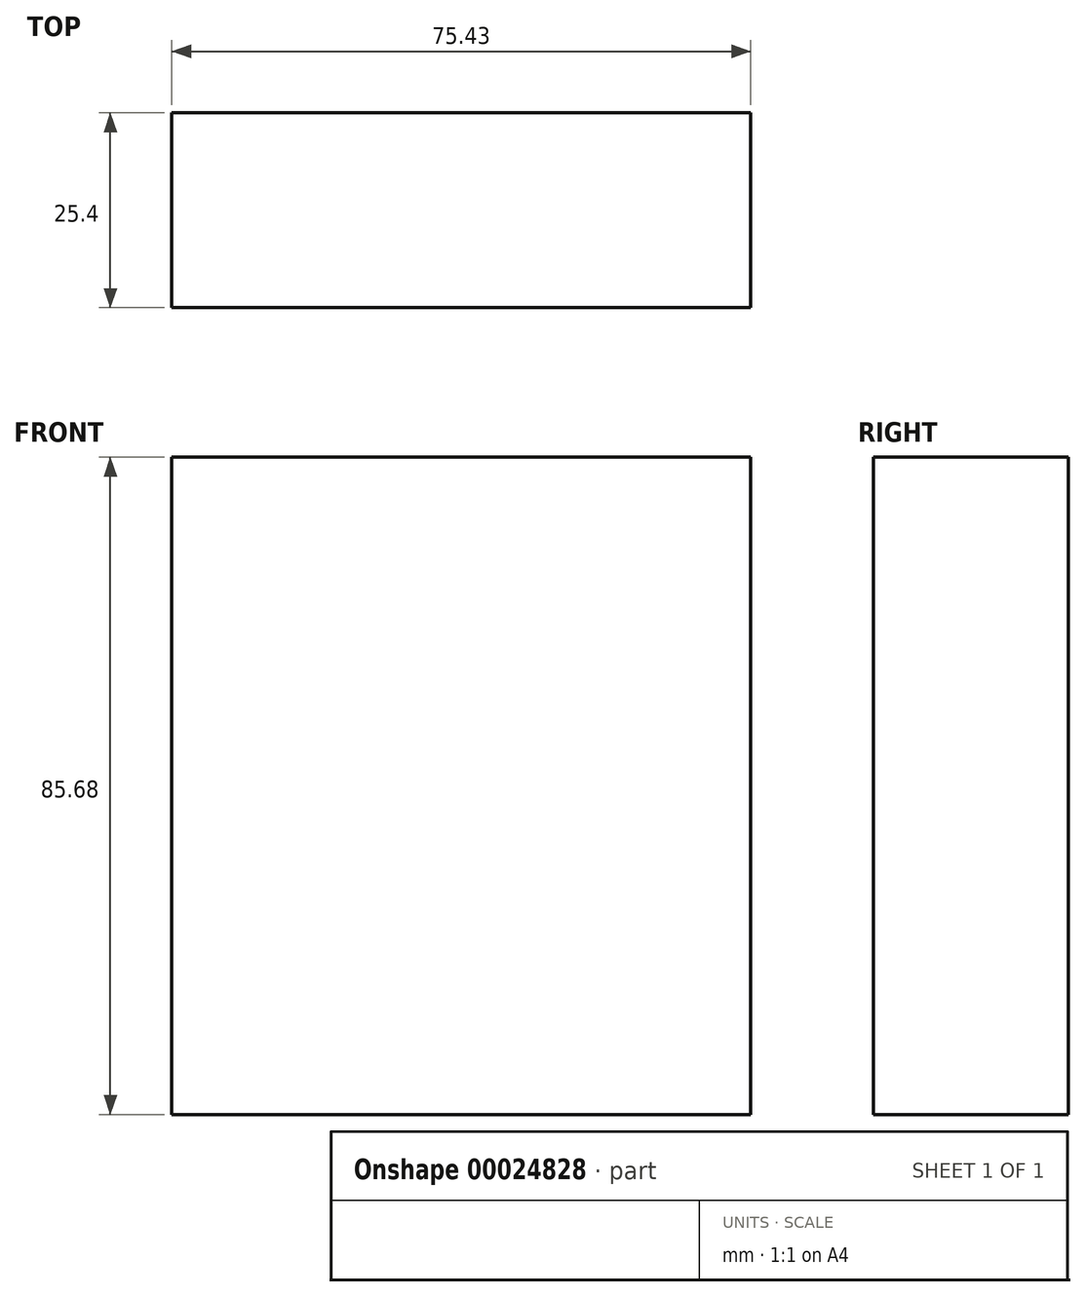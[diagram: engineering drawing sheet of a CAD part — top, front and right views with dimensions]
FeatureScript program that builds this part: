
annotation { "Feature Type Name" : "Feature", "Feature Type Description" : "" }
export const myFeature = defineFeature(function(context is Context, id is Id, definition is map)
    precondition{}
    {
        {
            var Q0;
            Q0=qCreatedBy(makeId("Front.planeOp"),FACE);
            var sketch = newSketch(context, id + "F0", { "sketchPlane" : qUnion([Q0])});
            skLineSegment(sketch, "E0.bottom", {"start": v(-44.26, 49.4) * mm, "end": v(31.17, 49.4) * mm});
            skLineSegment(sketch, "E0.top", {"start": v(-44.26, -36.3) * mm, "end": v(31.17, -36.3) * mm});
            skLineSegment(sketch, "E0.left", {"start": v(-44.26, 49.4) * mm, "end": v(-44.26, -36.3) * mm});
            skLineSegment(sketch, "E0.right", {"start": v(31.17, 49.4) * mm, "end": v(31.17, -36.3) * mm});
            skSolve(sketch);
        }
        {
            var Q0;
            Q0=makeQuery(id+"F0.imprint","IMPRINT",FACE,{"disambiguationData":[TD([[makeQuery(id+"F0.imprint","IMPRINT",EDGE,{"derivedFrom":sQuery(id+"F0.wireOp",EDGE,"E0.bottom")}),-1.0]])]});
            extrude(context, id + "F1", {"entities" : qUnion([Q0]), "depth" : 25.4 * mm});
        }
        {
            var Q0;
            Q0=makeQuery(id+"F1.opExtrude","CAP_FACE",FACE,{"disambiguationData":[OSD([sQuery(id+"F0.wireOp",EDGE,"E0.bottom"),sQuery(id+"F0.wireOp",EDGE,"E0.top"),sQuery(id+"F0.wireOp",EDGE,"E0.left"),sQuery(id+"F0.wireOp",EDGE,"E0.right")])],"isStart":false});
            var sketch = newSketch(context, id + "F2", { "sketchPlane" : qUnion([Q0])});
            skCircle(sketch, "E1", {"center": v(-10.52, 13.9) * mm, "radius": 22.9 * mm});
            skSolve(sketch);
        }
        {
            var Q0;
            Q0=sQuery(id+"F2.wireOp",EDGE,"E1");
            var Q1;
            Q1=makeQuery(id+"F1.opExtrude","CAP_EDGE",EDGE,{"disambiguationData":[OSD([sQuery(id+"F0.wireOp",EDGE,"E0.bottom")])],"isStart":false});
            revolve(context, id + "F3", {"bodyType" : ToolBodyType.SURFACE, "surfaceEntities" : qUnion([Q0]), "axis" : qUnion([Q1]), "revolveType" : RevolveType.ONE_DIRECTION, "oppositeDirection" : true, "angle" : 60 * degree});
        }
    });
